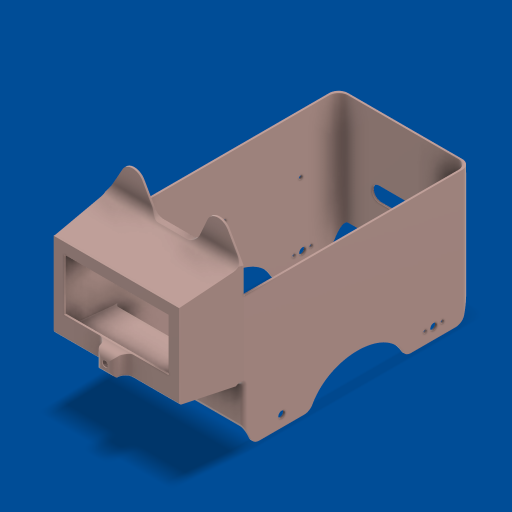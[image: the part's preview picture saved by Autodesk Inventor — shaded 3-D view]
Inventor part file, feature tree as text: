
AUTODESK INVENTOR PART (.ipt)
format: ipt  version: 2023.1 (Build 271208000, 208)  size: 588,800 bytes
history: native  units: mm
features: sketch x15, extrude x9, fillet x9, projected_geometry x8, plane x3, loft x1, shell x1, split x1
ambient origin geometry x8: Origin, YZ Plane, XZ Plane, XY Plane, X Axis, Y Axis, Z Axis, Center Point
bodies: Solid1 (feature_tree)
feature tree (47):
  extrude  "Extrusion1"  Depth=120.0mm
  plane  "Work Plane3"
  sketch  "Sketch3"  dims[d2=35.0mm d3=60.0mm]
  plane  "Work Plane4"
  loft  "Loft1"
  extrude  "roda"  Depth=70.0mm TaperAngle=0.0deg
  shell  "Shell1"  Thickness=1.0mm
  extrude  "Extrusion4"  Depth=1.0mm
  extrude  "Extrusion5"  TaperAngle=0.0deg  [1 undecoded]
  extrude  "Extrusion6"  Depth=1.0mm
  plane  "Work Plane5"
  fillet  "Fillet1"  Radius=9.0mm
  fillet  "Fillet2"  Radius=1.8mm
  fillet  "Fillet3"  Radius=1.8mm
  extrude  "Extrusion7"  TaperAngle=0.0deg  [1 undecoded]
  sketch  "Sketch9"  dims[d31=55.0mm d32=4.499175mm]
  sketch  "Sketch10"  dims[d33=63.99835mm d34=30.0mm]
  split  "Split1"
  fillet  "Fillet4"  Radius=3.5mm
  sketch  "Sketch12"  dims[d41=3.0mm]
  fillet  "Fillet5"  Radius=52.0mm
  fillet  "Fillet6"  Radius=5.8mm
  fillet  "Fillet7"  Radius=10.2mm
  sketch  "Sketch13"  dims[d45=9.0mm]
  fillet  "Fillet8"  Radius=1.0mm
  sketch  "Sketch14"  dims[d46=9.0mm]
  extrude  "Extrusion8"  Depth=4.499175mm
  extrude  "Extrusion9"  Depth=30.0mm
  extrude  "Extrusion10"  Depth=3.5mm
  fillet  "Fillet9"  Radius=6.0mm
  sketch  "Sketch1"  dims[d0=70.0mm d1=120.0mm]
  sketch  "Sketch4"  dims[d4=1.0mm d5=70.0mm d6=0.0mm d9=1.0mm]
  sketch  "Sketch5"  dims[d10=30.0mm d11=1.0mm]
  sketch  "Sketch6"  dims[d12=46.5mm d13=0.0mm d14=90.0deg]
  sketch  "Sketch7"  dims[d15=0.0mm d16=90.0deg d17=1.0mm d18=9.0mm d19=1.8mm d20=1.8mm]
  sketch  "Sketch8"  dims[d21=4.5mm d22=0.0mm d23=0.0mm d24=3.5mm d25=52.0mm d27=5.8mm d28=10.2mm d29=1.0mm d30=0.0mm]
  projected_geometry  "Projected Loop1"
  projected_geometry  "Projected Loop2"
  projected_geometry  "Projected Loop3"
  projected_geometry  "Projected Loop4"
  projected_geometry  "Projected Loop5"
  sketch  "Sketch11"  dims[d36=6.0mm d38=3.5mm d40=6.0mm]
  projected_geometry  "Projected Loop6"
  projected_geometry  "Projected Loop7"
  projected_geometry  "Projected Loop8"
  sketch  "Sketch15"  dims[d47=0.6mm]
  sketch  "Sketch16"  dims[d48=6.0mm d49=-0.174533mm d50=0.4mm d51=0.0mm d52=4.05mm d53=3.0mm d54=3.0mm d55=3.0mm d56=4.0mm d57=0.4mm d58=0.0mm d59=20.0mm d60=20.0mm d61=35.0mm d62=35.0mm d64=100.0mm d65=1.745329mm d66=5.0mm d67=2.0mm d68=2.0mm d69=5.0mm d70=2.0mm d71=2.0mm d72=2.0mm d73=40.0mm d74=40.0mm d75=20.0mm d76=10.0mm d77=0.0mm d78=4.0mm d79=33.0mm d80=25.0mm d81=10.0mm d82=0.0mm d83=12.0mm d84=12.0mm d85=45.0mm d86=10.0mm d87=70.0mm d88=12.5mm d89=1.0mm d90=0.0mm d91=5.0mm]
note: 2 required parameter values undecoded (feature->parameter linkage not recoverable at this tier; creation-order binding heuristic only, values carry confidence <= 0.55)
